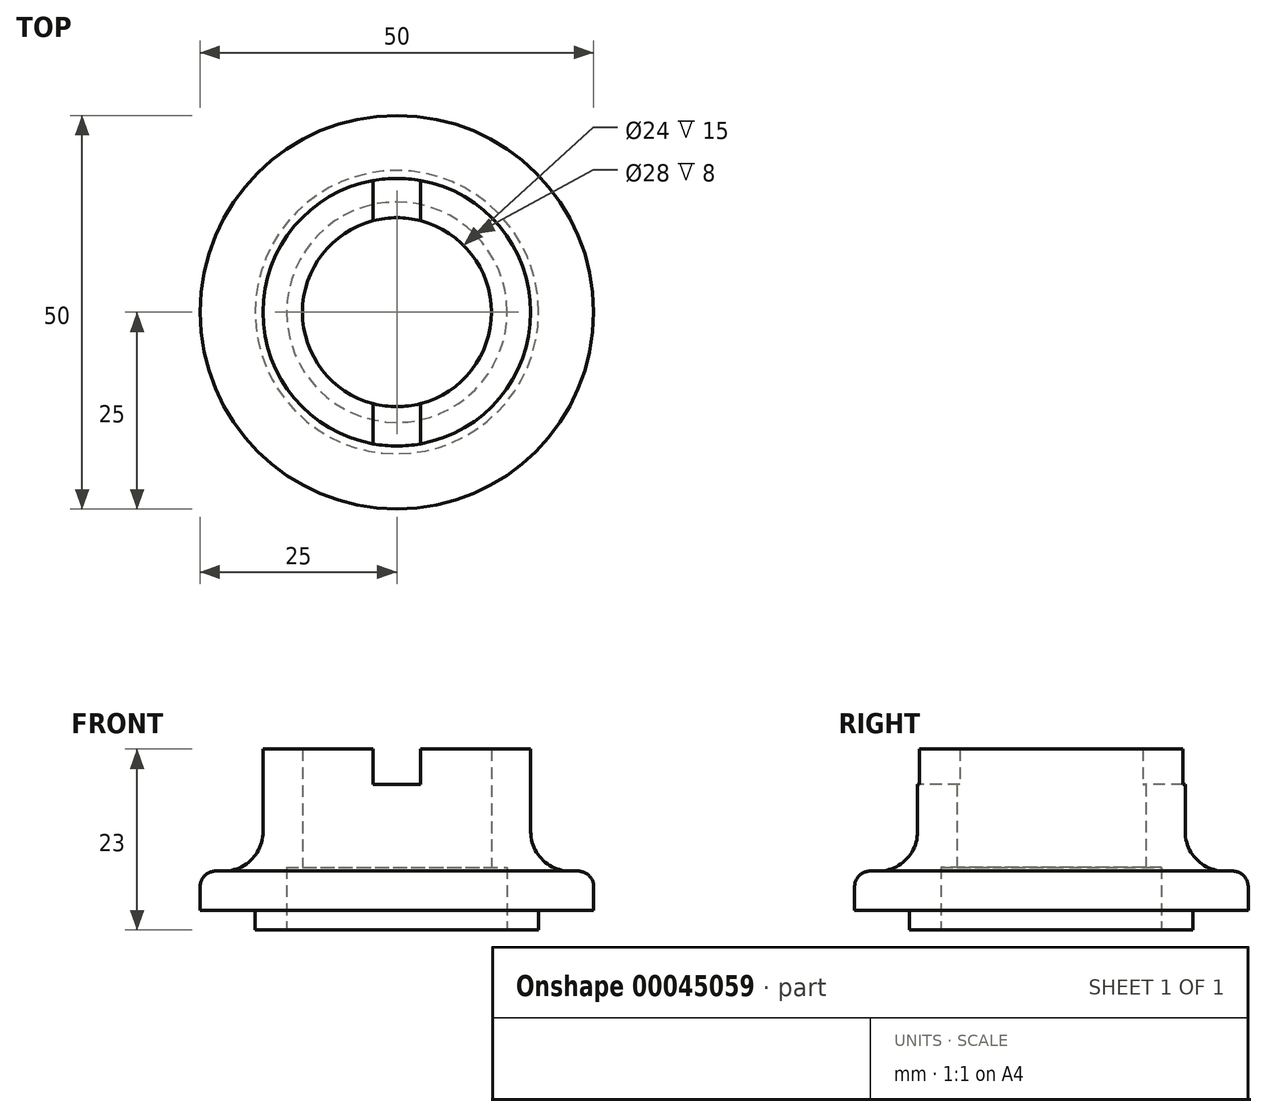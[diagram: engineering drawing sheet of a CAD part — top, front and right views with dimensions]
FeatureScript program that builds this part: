
annotation { "Feature Type Name" : "Feature", "Feature Type Description" : "" }
export const myFeature = defineFeature(function(context is Context, id is Id, definition is map)
    precondition{}
    {
        {
            var Q0;
            Q0=qCreatedBy(makeId("Front.planeOp"),FACE);
            var sketch = newSketch(context, id + "F0", { "sketchPlane" : qUnion([Q0])});
            skLineSegment(sketch, "E0", {"start": v(0, 0) * mm, "end": v(0, 38.08) * mm, "construction": true});
            skLineSegment(sketch, "E1", {"start": v(14, 0) * mm, "end": v(14, 8) * mm});
            skLineSegment(sketch, "E2", {"start": v(14, 8) * mm, "end": v(12, 8) * mm});
            skLineSegment(sketch, "E3", {"start": v(12, 8) * mm, "end": v(12, 23) * mm});
            skLineSegment(sketch, "E4", {"start": v(12, 23) * mm, "end": v(17, 23) * mm});
            skLineSegment(sketch, "E5", {"start": v(17, 23) * mm, "end": v(17, 12.5) * mm});
            skLineSegment(sketch, "E6", {"start": v(22, 7.5) * mm, "end": v(23, 7.5) * mm});
            skLineSegment(sketch, "E7", {"start": v(25, 5.5) * mm, "end": v(25, 2.5) * mm});
            skLineSegment(sketch, "E8", {"start": v(25, 2.5) * mm, "end": v(18, 2.5) * mm});
            skLineSegment(sketch, "E9", {"start": v(18, 2.5) * mm, "end": v(18, 0) * mm});
            skLineSegment(sketch, "E10", {"start": v(18, 0) * mm, "end": v(14, 0) * mm});
            skPoint(sketch, "E11.visualSharp", {"position": v(17, 7.5) * mm});
            skArc(sketch, "E11.filletArc", {"start": v(17, 12.5) * mm, "mid": v(18.46, 8.96) * mm, "end": v(22, 7.5) * mm});
            skPoint(sketch, "E12.visualSharp", {"position": v(25, 7.5) * mm});
            skArc(sketch, "E12.filletArc", {"start": v(25, 5.5) * mm, "mid": v(24.41, 6.91) * mm, "end": v(23, 7.5) * mm});
            skLineSegment(sketch, "E13", {"start": v(0, 23) * mm, "end": v(3, 23) * mm});
            skLineSegment(sketch, "E14", {"start": v(3, 23) * mm, "end": v(3, 18.5) * mm});
            skLineSegment(sketch, "E15", {"start": v(3, 18.5) * mm, "end": v(-3, 18.5) * mm});
            skLineSegment(sketch, "E16", {"start": v(-3, 18.5) * mm, "end": v(-3, 23) * mm});
            skLineSegment(sketch, "E17", {"start": v(-3, 23) * mm, "end": v(0, 23) * mm});
            skSolve(sketch);
        }
        {
            var Q0;
            Q0=makeQuery(id+"F0.imprint","IMPRINT",FACE,{"disambiguationData":[TD([[makeQuery(id+"F0.imprint","IMPRINT",EDGE,{"derivedFrom":sQuery(id+"F0.wireOp",EDGE,"E1")}),-1.0]])]});
            var Q1;
            Q1=sQuery(id+"F0.wireOp",EDGE,"E0");
            revolve(context, id + "F1", {"entities" : qUnion([Q0]), "axis" : qUnion([Q1]), "revolveType" : RevolveType.FULL});
        }
        {
            var Q0;
            Q0=makeQuery(id+"F0.imprint","IMPRINT",FACE,{"disambiguationData":[TD([[makeQuery(id+"F0.imprint","IMPRINT",EDGE,{"derivedFrom":sQuery(id+"F0.wireOp",EDGE,"E13")}),-1.0]])]});
            extrude(context, id + "F2", {"entities" : qUnion([Q0]), "operationType" : NewBodyOperationType.REMOVE, "endBound" : BoundingType.THROUGH_ALL, "oppositeDirection" : true, "depth" : 25 * mm, "hasSecondDirection" : true, "secondDirectionBound" : SecondDirectionBoundingType.THROUGH_ALL, "secondDirectionOppositeDirection" : false, "secondDirectionDepth" : 25 * mm});
        }
    });
